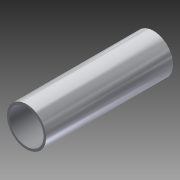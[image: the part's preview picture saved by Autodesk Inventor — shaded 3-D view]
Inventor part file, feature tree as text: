
AUTODESK INVENTOR PART (.ipt)
format: ipt  version: 2015 (Build 190159000, 159)  size: 87,552 bytes
history: native  units: in
note: dims shown in document units (in); Inventor stores cm internally (conversion verified against a paired STEP export)
features: extrude x1, sketch x1
ambient origin geometry x8: Origin, YZ Plane, XZ Plane, XY Plane, X Axis, Y Axis, Z Axis, Center Point
bodies: Solid1 (feature_tree)
feature tree (2):
  extrude  "Extrusion1"  Depth=1.625in
  sketch  "Sketch1"  dims[d0=0.5in d1=0.03in d2=1.625in d3=0.0in]
